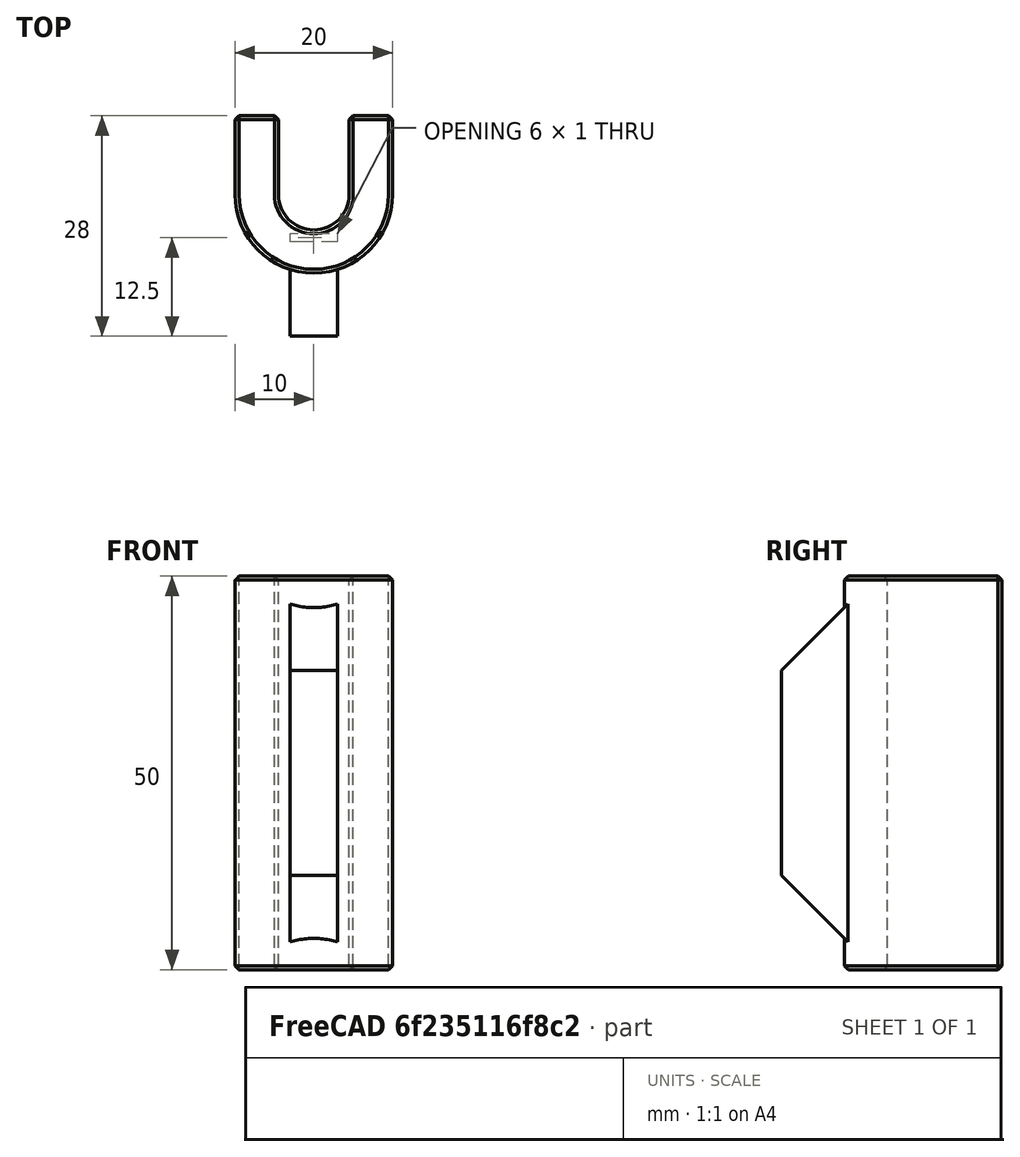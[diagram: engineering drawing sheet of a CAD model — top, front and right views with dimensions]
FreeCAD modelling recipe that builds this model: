
FCSTD DOCUMENT  (FreeCAD 0.18R14555 (Git shallow))
Label: gantry-leleling-helper
License: All rights reserved
LicenseURL: http://en.wikipedia.org/wiki/All_rights_reserved
objects: Part::Box×3, Part::MultiFuse×3, Part::Chamfer×3, Part::Cylinder×2, Part::Cut×1
note: 12 computed .brp shape members not serialized (recipe doc carries the construction recipe); baked Part::Feature solids carry a one-line shape summary decoded from their .brp

FEATURE [Part::Cylinder] Cylinder
  Angle = 360
  AttacherType = Attacher::AttachEngine3D
  Height = 50
  Radius = 4.5
FEATURE [Part::Cylinder] Cylinder001
  Angle = 360
  AttacherType = Attacher::AttachEngine3D
  Height = 50
  Radius = 10
FEATURE [Part::Box] Box  label="Cube"
  AttacherType = Attacher::AttachEngine3D
  Height = 50
  Length = 20
  Placement = pos=(-10,0,0) rot=(0,0,1;0rad)
  Width = 10
FEATURE [Part::MultiFuse] Fusion
  Shapes = -> [Box,Cylinder001]
FEATURE [Part::Box] Box001  label="Cube001"
  AttacherType = Attacher::AttachEngine3D
  Height = 50
  Length = 9
  Placement = pos=(-4.5,0,0) rot=(0,0,1;0rad)
  Width = 10
FEATURE [Part::MultiFuse] Fusion001
  Shapes = -> [Box001,Cylinder]
FEATURE [Part::Cut] Cut
  Base = -> Fusion
  Tool = -> Fusion001
FEATURE [Part::Box] Box002  label="Cube002"
  AttacherType = Attacher::AttachEngine3D
  Height = 50
  Length = 6
  Placement = pos=(-3,-18,0) rot=(0,0,1;0rad)
  Width = 13
FEATURE [Part::Chamfer] Chamfer
  Base = -> Box002
  Edges = 1 edges r=12: [Edge10]
FEATURE [Part::Chamfer] Chamfer001
  Base = -> Chamfer
  Edges = 1 edges r=12: [Edge8]
FEATURE [Part::MultiFuse] Fusion002
  Shapes = -> [Chamfer001,Cut]
FEATURE [Part::Chamfer] Chamfer002
  Base = -> Fusion002
  Edges = 24 edges r=0.5: [Edge10,Edge13,Edge18,Edge24,Edge25,Edge26,Edge27,Edge28,Edge29,Edge31,Edge37,Edge42,Edge43,Edge44,Edge45,Edge46,Edge47,Edge49,Edge50,Edge51,Edge52,Edge54,Edge55,Edge56]
